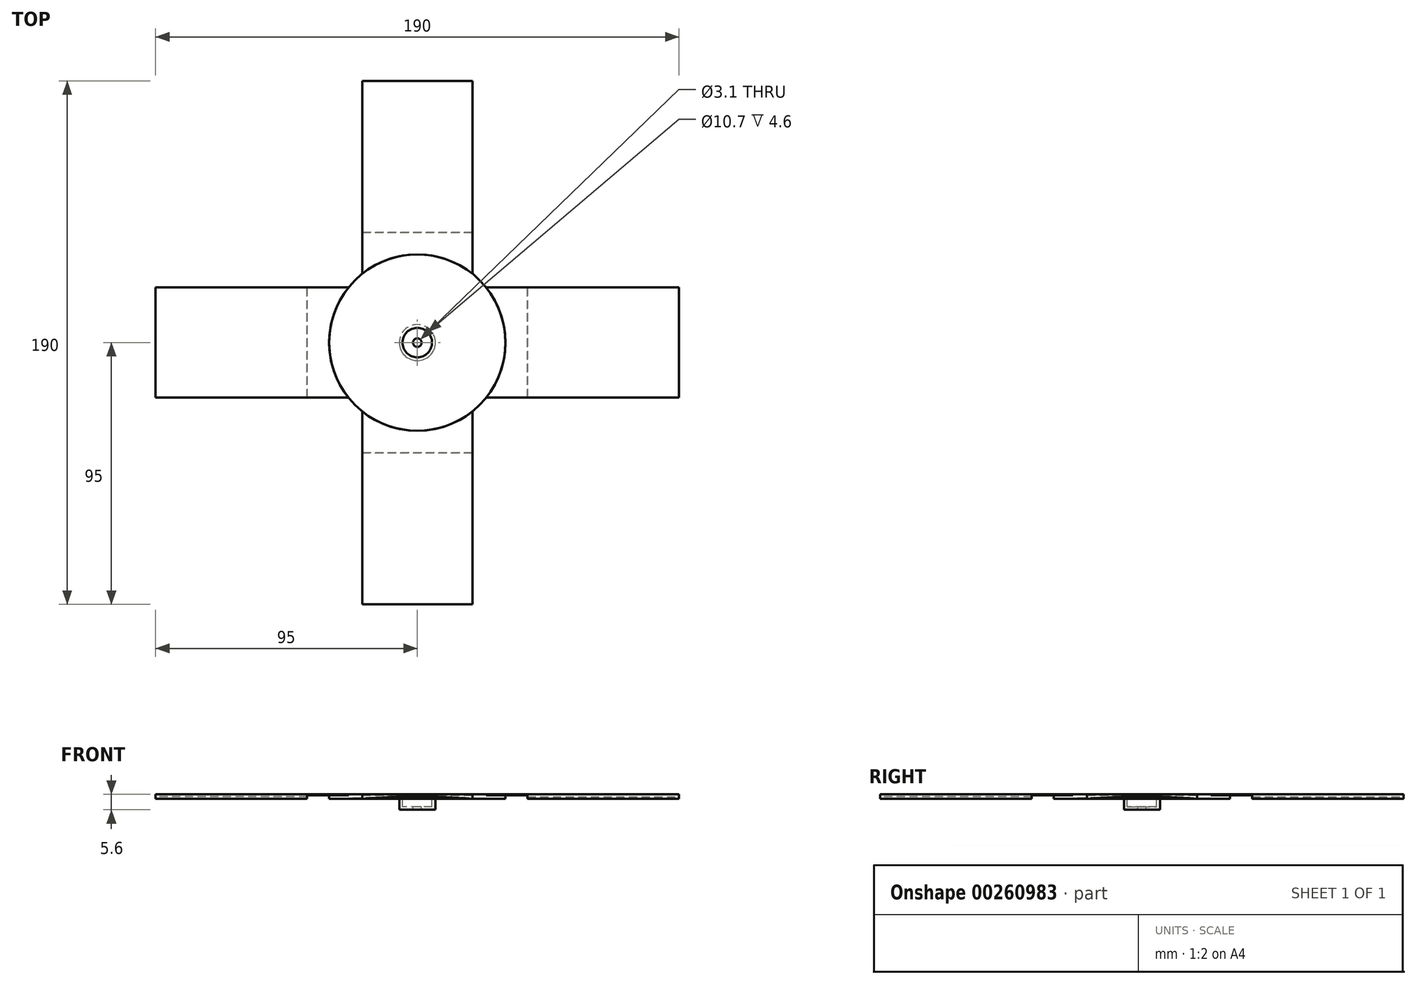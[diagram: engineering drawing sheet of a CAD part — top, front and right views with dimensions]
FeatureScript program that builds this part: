
annotation { "Feature Type Name" : "Feature", "Feature Type Description" : "" }
export const myFeature = defineFeature(function(context is Context, id is Id, definition is map)
    precondition{}
    {
        {
            var Q0;
            Q0=qCreatedBy(makeId("Front.planeOp"),FACE);
            var sketch = newSketch(context, id + "F0", { "sketchPlane" : qUnion([Q0])});
            skLineSegment(sketch, "E0", {"start": v(32, 0) * mm, "end": v(32, 0.8) * mm});
            skPoint(sketch, "E1.orphan", {"position": v(0, 1.2) * mm});
            skLineSegment(sketch, "E2", {"start": v(0, 0) * mm, "end": v(0, 1.2) * mm, "construction": true});
            skLineSegment(sketch, "E3", {"start": v(1.55, 1.2) * mm, "end": v(1.55, 0.8) * mm});
            skLineSegment(sketch, "E4", {"start": v(1.55, 0.8) * mm, "end": v(1.55, 1.6) * mm});
            skLineSegment(sketch, "E5", {"start": v(32, 0.8) * mm, "end": v(32, 1.6) * mm});
            skLineSegment(sketch, "E6", {"start": v(32, 1.6) * mm, "end": v(1.55, 1.6) * mm});
            skLineSegment(sketch, "E7", {"start": v(1.55, 0.8) * mm, "end": v(32, 0) * mm});
            skLineSegment(sketch, "E8", {"start": v(1.55, 1.6) * mm, "end": v(0, 1.6) * mm, "construction": true});
            skSolve(sketch);
        }
        {
            var Q0;
            Q0=makeQuery(id+"F0.imprint","IMPRINT",FACE,{"disambiguationData":[TD([[makeQuery(id+"F0.imprint","IMPRINT",EDGE,{"derivedFrom":sQuery(id+"F0.wireOp",EDGE,"E0")}),1.0]])]});
            var Q1;
            Q1=sQuery(id+"F0.wireOp",EDGE,"E2");
            revolve(context, id + "F1", {"entities" : qUnion([Q0]), "axis" : qUnion([Q1]), "revolveType" : RevolveType.FULL});
        }
        {
            var Q0;
            Q0=makeQuery(id+"F1.opRevolve","SWEPT_FACE",FACE,{"disambiguationData":[OSD([sQuery(id+"F0.wireOp",EDGE,"E6")])]});
            var sketch = newSketch(context, id + "F2", { "sketchPlane" : qUnion([Q0])});
            skLineSegment(sketch, "E9", {"start": v(0, 0) * mm, "end": v(0, 10) * mm, "construction": true});
            skLineSegment(sketch, "E10", {"start": v(100, 10) * mm, "end": v(100, -20) * mm});
            skLineSegment(sketch, "E11", {"start": v(100, -20) * mm, "end": v(24.98, -20) * mm});
            skCircle(sketch, "E12.0", {"center": v(0, 0) * mm, "radius": 32 * mm});
            skLineSegment(sketch, "E13", {"start": v(100, 10) * mm, "end": v(100, 20) * mm});
            skLineSegment(sketch, "E14", {"start": v(100, 20) * mm, "end": v(24.98, 20) * mm});
            skSolve(sketch);
        }
        {
            var Q0;
            Q0=makeQuery(id+"F2.imprint","IMPRINT",FACE,{"disambiguationData":[TD([[makeQuery(id+"F2.imprint","IMPRINT",EDGE,{"derivedFrom":sQuery(id+"F2.wireOp",EDGE,"E10")}),-1.0]])]});
            extrude(context, id + "F3", {"entities" : qUnion([Q0]), "oppositeDirection" : true, "depth" : .4 * mm});
        }
        {
            var Q0;
            Q0=qCreatedBy(makeId("Right.planeOp"),FACE);
            var sketch = newSketch(context, id + "F4", { "sketchPlane" : qUnion([Q0])});
            skLineSegment(sketch, "E15", {"start": v(0, -0.57) * mm, "end": v(0, 9.43) * mm});
            skSolve(sketch);
        }
        {
            var Q0;
            Q0=qCreatedBy(makeId("Front.planeOp"),FACE);
            var sketch = newSketch(context, id + "F5", { "sketchPlane" : qUnion([Q0])});
            skLineSegment(sketch, "E16", {"start": v(0, 0) * mm, "end": v(0, -20) * mm, "construction": true});
            skLineSegment(sketch, "E17", {"start": v(0, -20) * mm, "end": v(1.55, -20) * mm, "construction": true});
            skLineSegment(sketch, "E18", {"start": v(1.55, -20) * mm, "end": v(6.55, -20) * mm});
            skLineSegment(sketch, "E19", {"start": v(6.55, -20) * mm, "end": v(6.55, 0) * mm});
            skLineSegment(sketch, "E20", {"start": v(1.55, -20) * mm, "end": v(1.55, -18) * mm});
            skLineSegment(sketch, "E21", {"start": v(1.55, -18) * mm, "end": v(5.35, -18) * mm});
            skLineSegment(sketch, "E22", {"start": v(5.35, -18) * mm, "end": v(5.35, 0) * mm});
            skLineSegment(sketch, "E23", {"start": v(5.35, 0) * mm, "end": v(6.55, 0) * mm});
            skSolve(sketch);
        }
        {
            var Q0;
            Q0=makeQuery(id+"F5.imprint","IMPRINT",FACE,{"disambiguationData":[TD([[makeQuery(id+"F5.imprint","IMPRINT",EDGE,{"derivedFrom":sQuery(id+"F5.wireOp",EDGE,"E18")}),1.0]])]});
            var Q1;
            Q1=sQuery(id+"F5.wireOp",EDGE,"E16");
            revolve(context, id + "F6", {"entities" : qUnion([Q0]), "axis" : qUnion([Q1]), "revolveType" : RevolveType.FULL});
        }
        {
            var Q0;
            Q0=makeQuery(id+"F1.opRevolve","SWEPT_FACE",FACE,{"disambiguationData":[OSD([sQuery(id+"F0.wireOp",EDGE,"E6")])]});
            var sketch = newSketch(context, id + "F7", { "sketchPlane" : qUnion([Q0])});
            skCircle(sketch, "E24", {"center": v(0, 0) * mm, "radius": 6.55 * mm});
            skSolve(sketch);
        }
        {
            var Q0;
            Q0=makeQuery(id+"F7.imprint","IMPRINT",FACE,{"disambiguationData":[TD([[makeQuery(id+"F7.imprint","IMPRINT",EDGE,{"derivedFrom":sQuery(id+"F7.wireOp",EDGE,"E24")}),1.0]])]});
            extrude(context, id + "F8", {"entities" : qUnion([Q0]), "operationType" : NewBodyOperationType.ADD, "oppositeDirection" : true, "depth" : 1.6 * mm});
        }
        {
            var Q0;
            Q0=makeQuery(id+"F1.opRevolve","SWEPT_FACE",FACE,{"disambiguationData":[OSD([sQuery(id+"F0.wireOp",EDGE,"E6")])]});
            var sketch = newSketch(context, id + "F9", { "sketchPlane" : qUnion([Q0])});
            skCircle(sketch, "E25", {"center": v(0, 0) * mm, "radius": 5.35 * mm});
            skSolve(sketch);
        }
        {
            var Q0;
            Q0=makeQuery(id+"F9.imprint","IMPRINT",FACE,{"disambiguationData":[TD([[makeQuery(id+"F9.imprint","IMPRINT",EDGE,{"derivedFrom":sQuery(id+"F9.wireOp",EDGE,"E25")}),1.0]])]});
            extrude(context, id + "F10", {"entities" : qUnion([Q0]), "operationType" : NewBodyOperationType.REMOVE, "oppositeDirection" : true, "depth" : 10 * mm});
        }
        {
            var Q0;
            Q0=makeQuery(id+"F6.opRevolve","SWEPT_FACE",FACE,{"disambiguationData":[OSD([sQuery(id+"F5.wireOp",EDGE,"E18")])]});
            extrude(context, id + "F11", {"entities" : qUnion([Q0]), "operationType" : NewBodyOperationType.REMOVE, "oppositeDirection" : true, "depth" : 1 * mm});
        }
        {
            var Q0;
            Q0=makeQuery(id+"F3.opExtrude","SWEPT_FACE",FACE,{"disambiguationData":[OSD([sQuery(id+"F2.wireOp",EDGE,"E10"),sQuery(id+"F2.wireOp",EDGE,"E13")])]});
            extrude(context, id + "F12", {"entities" : qUnion([Q0]), "operationType" : NewBodyOperationType.ADD, "depth" : 30 * mm});
        }
        {
            var Q0;
            {var subQ0=sQuery(id+"F2.wireOp",EDGE,"E13");var subQ1=sQuery(id+"F2.wireOp",EDGE,"E10");Q0=makeQuery(id+"F12.boolean.opBoolean","MERGE",FACE,{"derivedFrom":[makeQuery(id+"F3.opExtrude","CAP_FACE",FACE,{"disambiguationData":[OSD([subQ1,sQuery(id+"F2.wireOp",EDGE,"E11"),sQuery(id+"F2.wireOp",EDGE,"E12.0"),subQ0,sQuery(id+"F2.wireOp",EDGE,"E14")])],"isStart":false}),makeQuery(id+"F12.opExtrude","SWEPT_FACE",FACE,{"disambiguationData":[OSD([subQ1,subQ0]),TDD([makeQuery(id+"F3.opExtrude","CAP_EDGE",EDGE,{"disambiguationData":[OSD([subQ1,subQ0])],"isStart":false})])]})]});}
            var sketch = newSketch(context, id + "F13", { "sketchPlane" : qUnion([Q0])});
            skLineSegment(sketch, "E26", {"start": v(130, 20) * mm, "end": v(40, 20) * mm});
            skLineSegment(sketch, "E27", {"start": v(40, 20) * mm, "end": v(40, -20) * mm});
            skLineSegment(sketch, "E28", {"start": v(40, -20) * mm, "end": v(130, -20) * mm});
            skLineSegment(sketch, "E29", {"start": v(130, -20) * mm, "end": v(130, 20) * mm});
            skSolve(sketch);
        }
        {
            var Q0;
            Q0=makeQuery(id+"F13.imprint","IMPRINT",FACE,{"disambiguationData":[TD([[makeQuery(id+"F13.imprint","IMPRINT",EDGE,{"derivedFrom":sQuery(id+"F13.wireOp",EDGE,"E26")}),1.0]])]});
            extrude(context, id + "F14", {"entities" : qUnion([Q0]), "operationType" : NewBodyOperationType.ADD, "depth" : 1.2 * mm});
        }
        {
            var Q0;
            Q0=makeQuery(id+"F14.boolean.opBoolean","MERGE",FACE,{"derivedFrom":[makeQuery(id+"F12.opExtrude","CAP_FACE",FACE,{"disambiguationData":[OSD([sQuery(id+"F2.wireOp",EDGE,"E10"),sQuery(id+"F2.wireOp",EDGE,"E13")])],"isStart":false}),makeQuery(id+"F14.opExtrude","SWEPT_FACE",FACE,{"disambiguationData":[OSD([sQuery(id+"F13.wireOp",EDGE,"E29")])]})]});
            var sketch = newSketch(context, id + "F15", { "sketchPlane" : qUnion([Q0])});
            skLineSegment(sketch, "E30.0", {"start": v(-20, 1.6) * mm, "end": v(20, 1.6) * mm, "construction": true});
            skLineSegment(sketch, "E31.0", {"start": v(-20, 0) * mm, "end": v(20, 0) * mm, "construction": true});
            skLineSegment(sketch, "E32", {"start": v(0, 1.6) * mm, "end": v(0, 0.8) * mm, "construction": true});
            skPoint(sketch, "E32.endSnap0", {"position": v(0, 1.6) * mm});
            skArc(sketch, "E33", {"start": v(20, 0) * mm, "mid": v(0, 0.8) * mm, "end": v(-20, 0) * mm});
            skSolve(sketch);
        }
        {
            var Q0;
            Q0=makeQuery(id+"F15.imprint","IMPRINT",FACE,{"disambiguationData":[TD([[makeQuery(id+"F15.imprint","IMPRINT",EDGE,{"derivedFrom":sQuery(id+"F15.wireOp",EDGE,"E33")}),1.0]])]});
            extrude(context, id + "F16", {"entities" : qUnion([Q0]), "operationType" : NewBodyOperationType.REMOVE, "oppositeDirection" : true, "depth" : 90 * mm});
        }
        {
            var Q0;
            Q0=makeQuery(id+"F6.opRevolve","SWEPT_FACE",FACE,{"disambiguationData":[OSD([sQuery(id+"F5.wireOp",EDGE,"E21")])]});
            extrude(context, id + "F17", {"entities" : qUnion([Q0]), "operationType" : NewBodyOperationType.ADD, "depth" : 15 * mm});
        }
        {
            var Q0;
            Q0=makeQuery(id+"F11.boolean.opBoolean","COPY",FACE,{"derivedFrom":makeQuery(id+"F11.opExtrude","CAP_FACE",FACE,{"disambiguationData":[OSD([sQuery(id+"F5.wireOp",EDGE,"E18")])],"isStart":false})});
            extrude(context, id + "F18", {"entities" : qUnion([Q0]), "operationType" : NewBodyOperationType.REMOVE, "oppositeDirection" : true, "depth" : 15 * mm});
        }
        {
            var Q0;
            Q0=makeQuery(id+"F14.boolean.opBoolean","MERGE",FACE,{"derivedFrom":[makeQuery(id+"F12.opExtrude","CAP_FACE",FACE,{"disambiguationData":[OSD([sQuery(id+"F2.wireOp",EDGE,"E10"),sQuery(id+"F2.wireOp",EDGE,"E13")])],"isStart":false}),makeQuery(id+"F14.opExtrude","SWEPT_FACE",FACE,{"disambiguationData":[OSD([sQuery(id+"F13.wireOp",EDGE,"E29")])]})]});
            extrude(context, id + "F19", {"entities" : qUnion([Q0]), "operationType" : NewBodyOperationType.REMOVE, "oppositeDirection" : true, "depth" : 35 * mm});
        }
        {
            var Q0;
            Q0=makeQuery(id+"F3.opExtrude","SWEPT_BODY",BODY,{"disambiguationData":[OSD([sQuery(id+"F2.wireOp",EDGE,"Gn05NFXd-evuW-6otC-wRoB-VLKZHpSgzgBO"),sQuery(id+"F2.wireOp",EDGE,"E10"),sQuery(id+"F2.wireOp",EDGE,"E11"),sQuery(id+"F2.wireOp",EDGE,"E12.0")])]});
            var Q1;
            Q1=sQuery(id+"F4.wireOp",EDGE,"E15");
            circularPattern(context, id + "F20", {"entities" : qUnion([Q0]), "axis" : qUnion([Q1]), "angle" : 360 * degree, "instanceCount" : 4, "equalSpace" : true});
        }
    });
